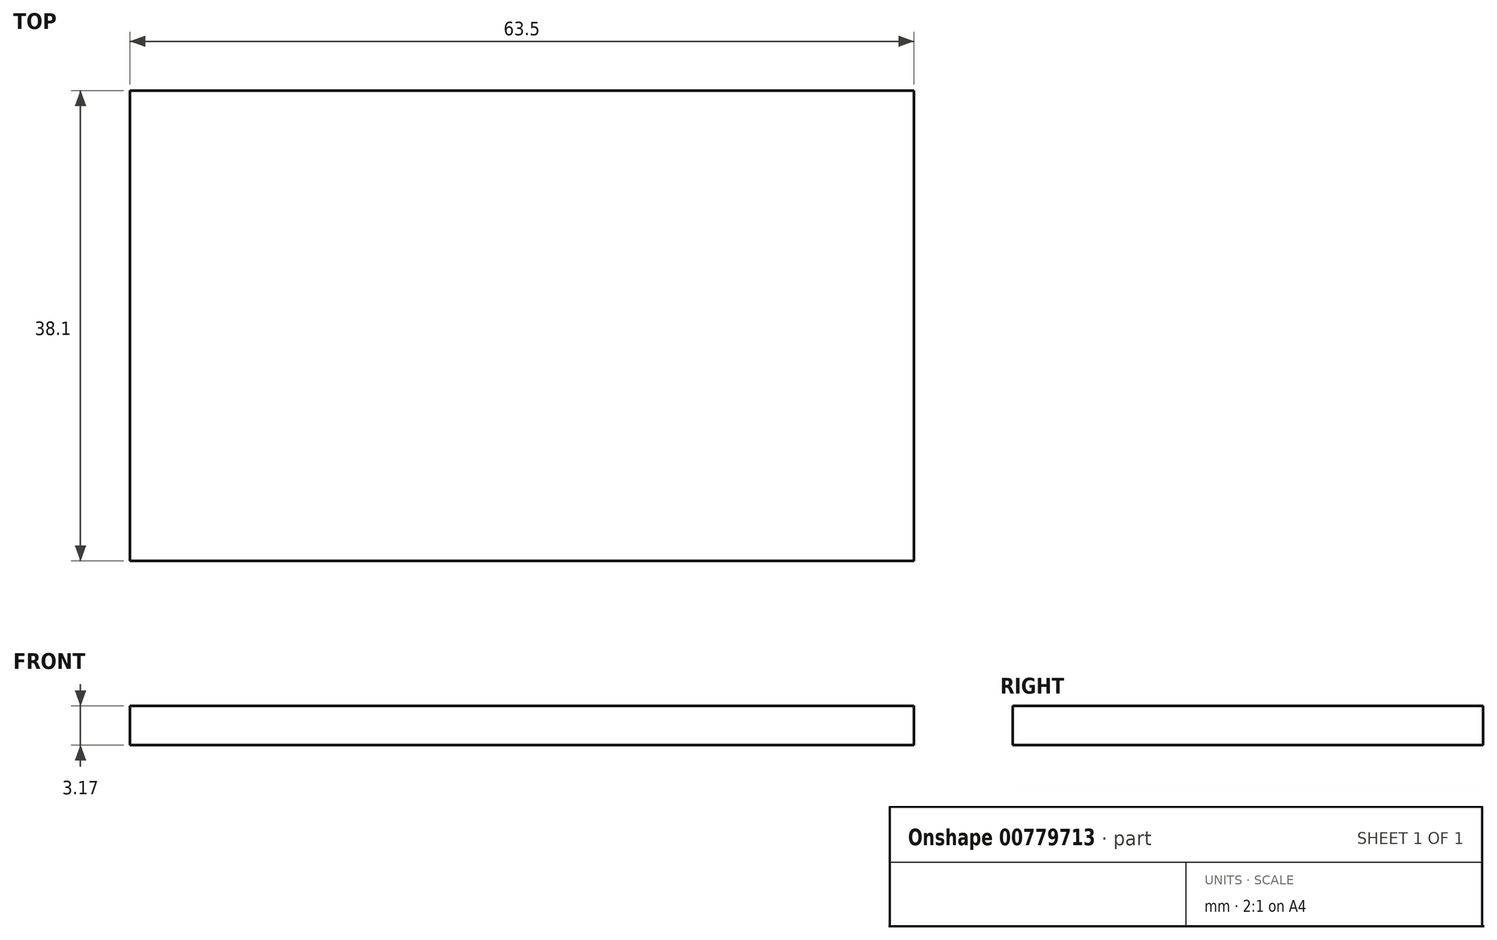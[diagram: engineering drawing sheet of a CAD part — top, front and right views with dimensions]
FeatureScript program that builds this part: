
annotation { "Feature Type Name" : "Feature", "Feature Type Description" : "" }
export const myFeature = defineFeature(function(context is Context, id is Id, definition is map)
    precondition{}
    {
        {
            var Q0;
            Q0=qCreatedBy(makeId("Top.planeOp"),FACE);
            var sketch = newSketch(context, id + "F0", { "sketchPlane" : qUnion([Q0])});
            skLineSegment(sketch, "E0.bottom", {"start": v(-19.99, 8.75) * mm, "end": v(43.51, 8.75) * mm});
            skLineSegment(sketch, "E0.top", {"start": v(-19.99, -29.35) * mm, "end": v(43.51, -29.35) * mm});
            skLineSegment(sketch, "E0.left", {"start": v(-19.99, 8.75) * mm, "end": v(-19.99, -29.35) * mm});
            skLineSegment(sketch, "E0.right", {"start": v(43.51, 8.75) * mm, "end": v(43.51, -29.35) * mm});
            skSolve(sketch);
        }
        {
            var Q0;
            Q0=makeQuery(id+"F0.imprint","IMPRINT",FACE,{"disambiguationData":[TD([[makeQuery(id+"F0.imprint","IMPRINT",EDGE,{"derivedFrom":sQuery(id+"F0.wireOp",EDGE,"E0.bottom")}),-1.0]])]});
            extrude(context, id + "F1", {"entities" : qUnion([Q0]), "depth" : 3.17 * mm, "offsetDistance" : 25.4 * mm});
        }
    });
